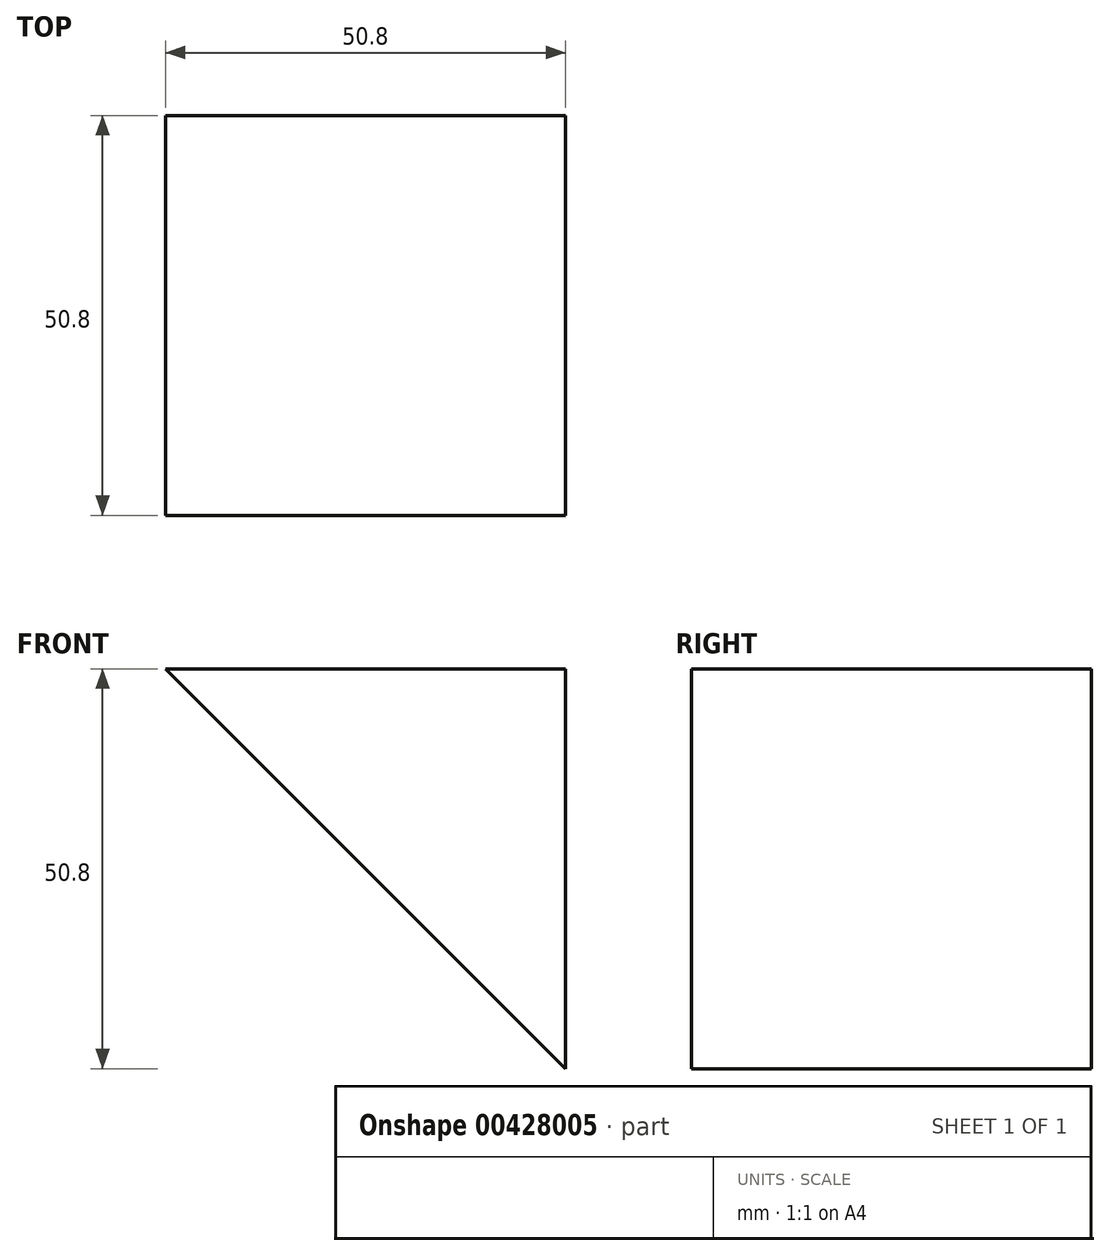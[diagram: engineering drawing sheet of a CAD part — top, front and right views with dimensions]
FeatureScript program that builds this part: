
annotation { "Feature Type Name" : "Feature", "Feature Type Description" : "" }
export const myFeature = defineFeature(function(context is Context, id is Id, definition is map)
    precondition{}
    {
        {
            var Q0;
            Q0=qCreatedBy(makeId("Front.planeOp"),FACE);
            var sketch = newSketch(context, id + "F0", { "sketchPlane" : qUnion([Q0])});
            skLineSegment(sketch, "E0.top", {"start": v(0, 50.8) * mm, "end": v(-50.8, 50.8) * mm});
            skLineSegment(sketch, "E0.left", {"start": v(0, 0) * mm, "end": v(0, 50.8) * mm});
            skLineSegment(sketch, "E1", {"start": v(-50.8, 50.8) * mm, "end": v(0, 0) * mm});
            skSolve(sketch);
        }
        {
            var Q0;
            Q0 = qSketchRegion(id + "F0", true);
            extrude(context, id + "F1", {"entities" : qUnion([Q0]), "depth" : 50.8 * mm});
        }
    });
